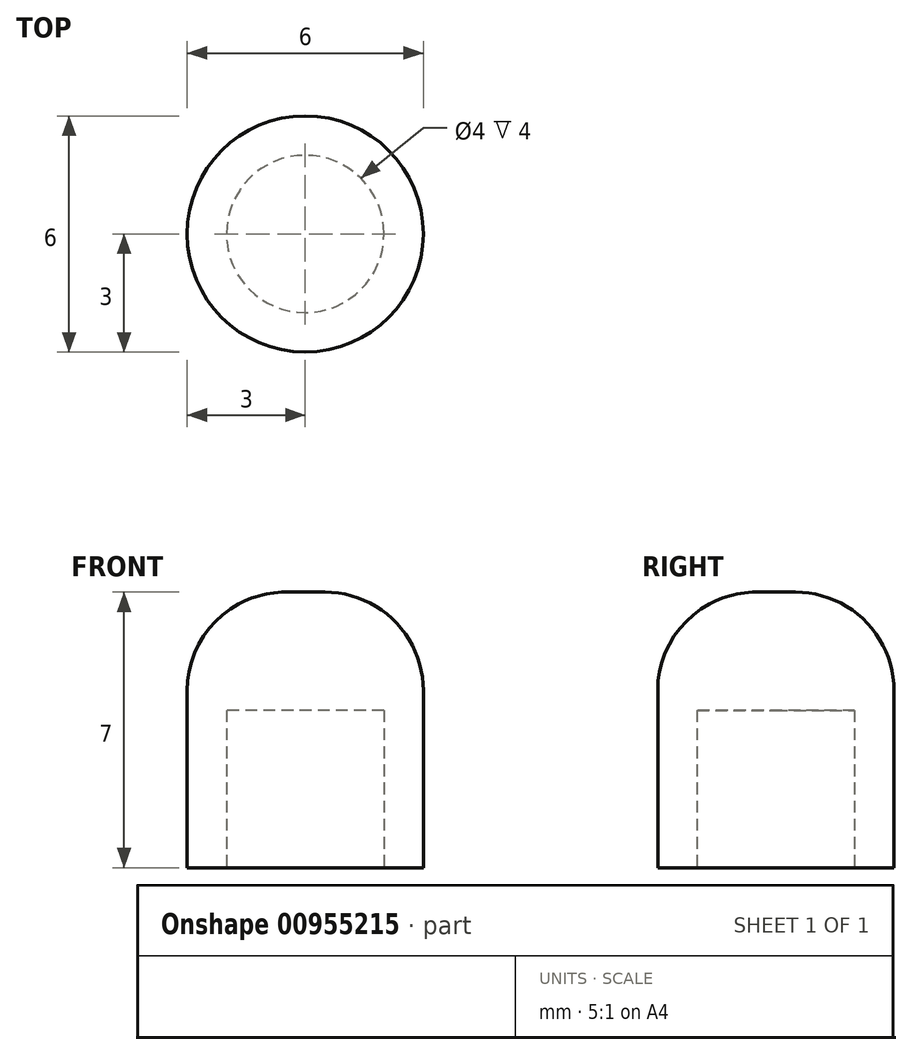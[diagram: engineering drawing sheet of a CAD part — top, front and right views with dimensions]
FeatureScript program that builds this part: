
annotation { "Feature Type Name" : "Feature", "Feature Type Description" : "" }
export const myFeature = defineFeature(function(context is Context, id is Id, definition is map)
    precondition{}
    {
        {
            var Q0;
            Q0=qCreatedBy(makeId("Top.planeOp"),FACE);
            var sketch = newSketch(context, id + "F0", { "sketchPlane" : qUnion([Q0])});
            skCircle(sketch, "E0", {"center": v(0, 0) * mm, "radius": 2 * mm});
            skCircle(sketch, "E1", {"center": v(0, 0) * mm, "radius": 3 * mm});
            skSolve(sketch);
        }
        {
            var Q0;
            Q0=makeQuery(id+"F0.imprint","IMPRINT",FACE,{"disambiguationData":[TD([[makeQuery(id+"F0.imprint","IMPRINT",EDGE,{"derivedFrom":sQuery(id+"F0.wireOp",EDGE,"E0")}),-1.0]])]});
            var Q1;
            Q1=makeQuery(id+"F0.imprint","IMPRINT",FACE,{"disambiguationData":[TD([[makeQuery(id+"F0.imprint","IMPRINT",EDGE,{"derivedFrom":sQuery(id+"F0.wireOp",EDGE,"E0")}),1.0]])]});
            extrude(context, id + "F1", {"entities" : qUnion([Q0, Q1]), "depth" : 7 * mm, "offsetDistance" : 25 * mm});
        }
        {
            var Q0;
            Q0=makeQuery(id+"F0.imprint","IMPRINT",FACE,{"disambiguationData":[TD([[makeQuery(id+"F0.imprint","IMPRINT",EDGE,{"derivedFrom":sQuery(id+"F0.wireOp",EDGE,"E0")}),1.0]])]});
            extrude(context, id + "F2", {"entities" : qUnion([Q0]), "operationType" : NewBodyOperationType.REMOVE, "depth" : 4 * mm, "offsetDistance" : 25 * mm});
        }
        {
            var Q0;
            Q0=makeQuery(id+"F1.opExtrude","CAP_FACE",FACE,{"disambiguationData":[OSD([sQuery(id+"F0.wireOp",EDGE,"E1")])],"isStart":false});
            fillet(context, id + "F3", {"entities" : qUnion([Q0]), "radius" : 2.5 * mm, "tangentPropagation" : true, "allowEdgeOverflow" : false});
        }
    });
